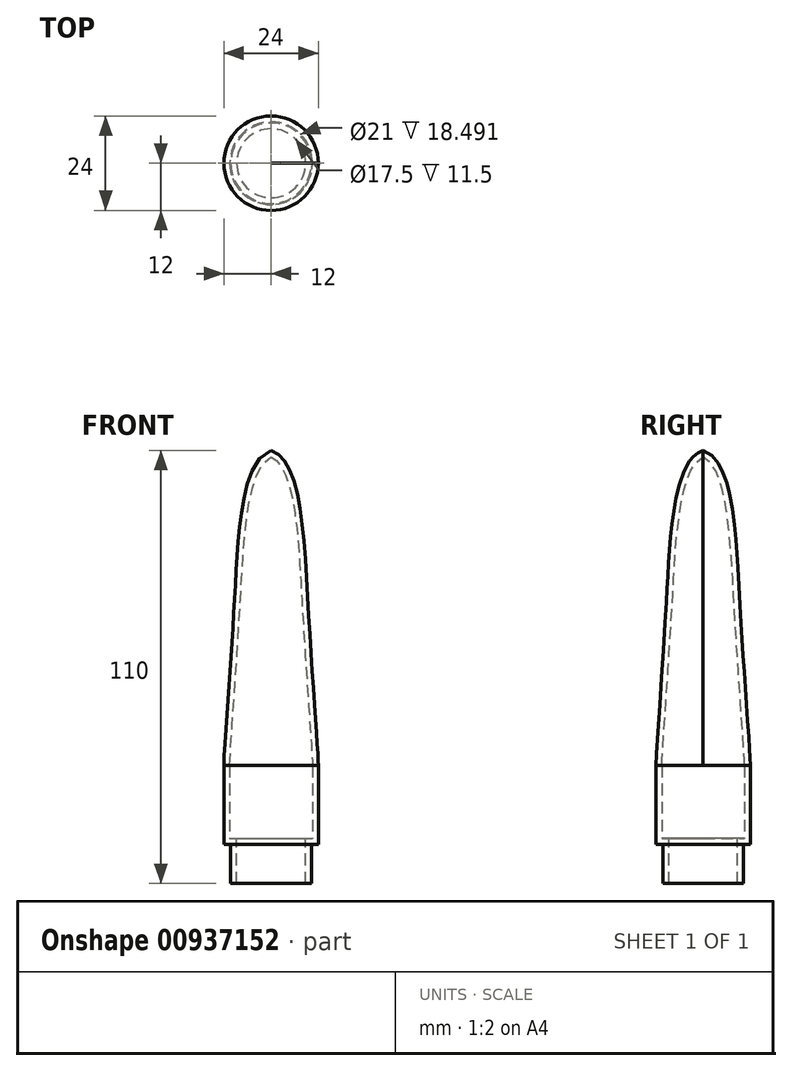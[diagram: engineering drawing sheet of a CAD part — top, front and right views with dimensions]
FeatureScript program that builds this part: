
annotation { "Feature Type Name" : "Feature", "Feature Type Description" : "" }
export const myFeature = defineFeature(function(context is Context, id is Id, definition is map)
    precondition{}
    {
        {
            var Q0;
            Q0=qCreatedBy(makeId("Front.planeOp"),FACE);
            var sketch = newSketch(context, id + "F0", { "sketchPlane" : qUnion([Q0])});
            skLineSegment(sketch, "E0", {"start": v(0, 0) * mm, "end": v(0, 100) * mm});
            skLineSegment(sketch, "E1", {"start": v(0, 0) * mm, "end": v(12, 0) * mm});
            skLineSegment(sketch, "E2", {"start": v(12, 0) * mm, "end": v(12, 20) * mm});
            skFitSpline(sketch, "E3", {"points": [v(0, 100) * mm, v(9.4, 60.53) * mm, v(12, 20) * mm], "startDerivative": vector(46.45, -15.12) * mm, "endDerivative": vector(0.23, -20.1) * mm});
            skLineSegment(sketch, "E4", {"start": v(0, 0) * mm, "end": v(0, 127.8) * mm, "construction": true});
            skSolve(sketch);
        }
        {
            var Q0;
            Q0 = qSketchRegion(id + "F0", true);
            var Q1;
            Q1=sQuery(id+"F0.wireOp",EDGE,"E4");
            revolve(context, id + "F1", {"surfaceOperationType" : NewSurfaceOperationType.NEW, "entities" : qUnion([Q0]), "axis" : qUnion([Q1]), "revolveType" : RevolveType.FULL});
        }
        {
            var Q0;
            Q0=makeQuery(id+"F1.opRevolve","SWEPT_FACE",FACE,{"disambiguationData":[OSD([sQuery(id+"F0.wireOp",EDGE,"E1")])]});
            var sketch = newSketch(context, id + "F2", { "sketchPlane" : qUnion([Q0])});
            skCircle(sketch, "E5", {"center": v(0, 0) * mm, "radius": 10.25 * mm});
            skSolve(sketch);
        }
        {
            var Q0;
            Q0 = qSketchRegion(id + "F2", true);
            extrude(context, id + "F3", {"entities" : qUnion([Q0]), "operationType" : NewBodyOperationType.ADD, "depth" : 10 * mm, "offsetDistance" : 25 * mm});
        }
        {
            var Q0;
            Q0=makeQuery(id+"F3.opExtrude","CAP_FACE",FACE,{"disambiguationData":[OSD([sQuery(id+"F2.wireOp",EDGE,"E5")])],"isStart":false});
            shell(context, id + "F4", {"entities" : qUnion([Q0]), "thickness" : 1.5 * mm});
        }
    });
